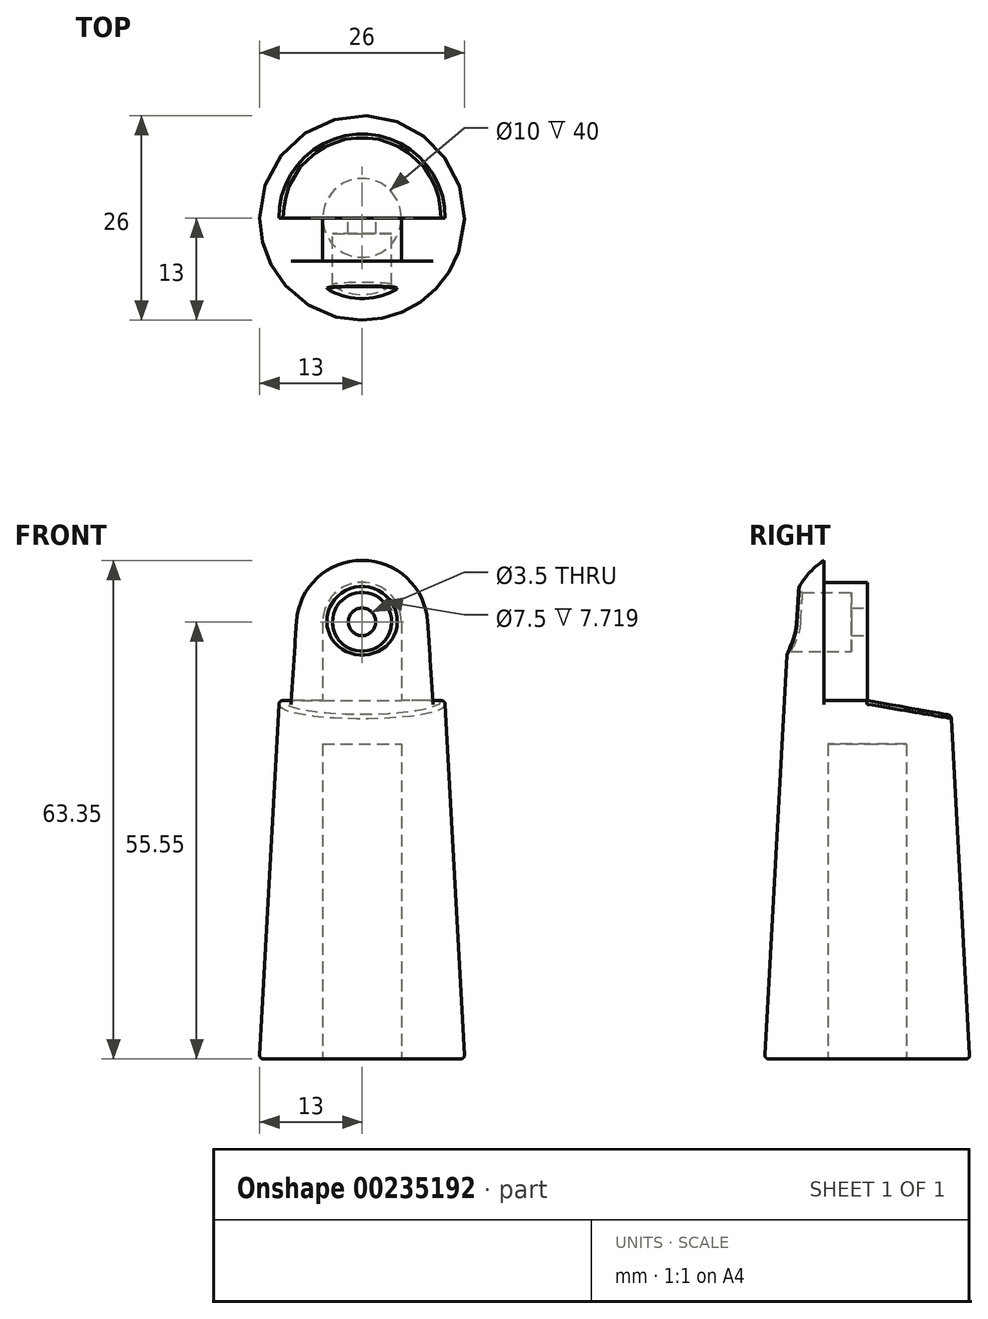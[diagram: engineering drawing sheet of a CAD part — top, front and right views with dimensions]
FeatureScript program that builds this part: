
annotation { "Feature Type Name" : "Feature", "Feature Type Description" : "" }
export const myFeature = defineFeature(function(context is Context, id is Id, definition is map)
    precondition{}
    {
        {
            var Q0;
            Q0=qCreatedBy(makeId("Front.planeOp"),FACE);
            var sketch = newSketch(context, id + "F0", { "sketchPlane" : qUnion([Q0])});
            skArc(sketch, "E0", {"start": v(0, 9.45) * mm, "mid": v(-6.87, 6.71) * mm, "end": v(-9.98, 0) * mm});
            skLineSegment(sketch, "E1", {"start": v(-9.98, 0) * mm, "end": v(-13.03, -55.55) * mm});
            skLineSegment(sketch, "E2", {"start": v(0, 9.45) * mm, "end": v(0, -55.55) * mm});
            skLineSegment(sketch, "E3", {"start": v(-13.03, -55.55) * mm, "end": v(0, -55.55) * mm});
            skSolve(sketch);
        }
        {
            var Q0;
            Q0 = qSketchRegion(id + "F0", true);
            var Q1;
            Q1=sQuery(id+"F0.wireOp",EDGE,"E2");
            revolve(context, id + "F1", {"entities" : qUnion([Q0]), "axis" : qUnion([Q1]), "revolveType" : RevolveType.FULL});
        }
        {
            var Q0;
            Q0=qCreatedBy(makeId("Right.planeOp"),FACE);
            var sketch = newSketch(context, id + "F2", { "sketchPlane" : qUnion([Q0])});
            skLineSegment(sketch, "E4", {"start": v(0, -10) * mm, "end": v(0, 17.7) * mm});
            skLineSegment(sketch, "E5", {"start": v(0, 17.7) * mm, "end": v(18.47, 17.7) * mm});
            skLineSegment(sketch, "E6", {"start": v(18.47, 17.7) * mm, "end": v(18.47, -13.26) * mm});
            skLineSegment(sketch, "E7", {"start": v(18.47, -13.26) * mm, "end": v(0, -10) * mm});
            skSolve(sketch);
        }
        {
            var Q0;
            Q0 = qSketchRegion(id + "F2", true);
            extrude(context, id + "F3", {"entities" : qUnion([Q0]), "operationType" : NewBodyOperationType.REMOVE, "endBound" : BoundingType.THROUGH_ALL, "oppositeDirection" : true, "depth" : 25 * mm, "hasSecondDirection" : true, "secondDirectionBound" : SecondDirectionBoundingType.THROUGH_ALL, "secondDirectionOppositeDirection" : false, "secondDirectionDepth" : 25 * mm});
        }
        {
            var Q0;
            Q0=qCreatedBy(makeId("Front.planeOp"),FACE);
            var sketch = newSketch(context, id + "F4", { "sketchPlane" : qUnion([Q0])});
            skLineSegment(sketch, "E8", {"start": v(0, 5) * mm, "end": v(0, -10) * mm, "construction": true});
            skArc(sketch, "E9", {"start": v(0, 5) * mm, "mid": v(-3.54, 3.54) * mm, "end": v(-5, 0) * mm});
            skLineSegment(sketch, "E10", {"start": v(-5, 0) * mm, "end": v(-5, -10) * mm});
            skLineSegment(sketch, "E11", {"start": v(-5, -10) * mm, "end": v(0, -10) * mm, "construction": true});
            skLineSegment(sketch, "E12.MirrorCS", {"start": v(5, -10) * mm, "end": v(0, -10) * mm, "construction": true});
            skLineSegment(sketch, "E13.MirrorCS", {"start": v(5, 0) * mm, "end": v(5, -10) * mm});
            skArc(sketch, "E14.MirrorCS", {"start": v(0, 5) * mm, "mid": v(3.54, 3.54) * mm, "end": v(5, 0) * mm});
            skLineSegment(sketch, "E15", {"start": v(-5, -10) * mm, "end": v(-22.67, -10) * mm});
            skLineSegment(sketch, "E16", {"start": v(-22.67, -10) * mm, "end": v(-22.67, 27.7) * mm});
            skLineSegment(sketch, "E17", {"start": v(-22.67, 27.7) * mm, "end": v(22.54, 27.7) * mm});
            skLineSegment(sketch, "E18", {"start": v(22.54, 27.7) * mm, "end": v(22.54, -10) * mm});
            skLineSegment(sketch, "E19", {"start": v(22.54, -10) * mm, "end": v(5, -10) * mm});
            skSolve(sketch);
        }
        {
            var Q0;
            Q0 = qSketchRegion(id + "F4", true);
            var Q1;
            Q1 = qConstructionFilter(qBodyType(qCreatedBy(id + "F4" ,EDGE), BodyType.WIRE), ConstructionObject.NO);
            extrude(context, id + "F5", {"entities" : qUnion([Q0]), "operationType" : NewBodyOperationType.REMOVE, "surfaceEntities" : qUnion([Q1]), "depth" : 5.5 * mm});
        }
        {
            var Q0;
            Q0=qCreatedBy(makeId("Front.planeOp"),FACE);
            var sketch = newSketch(context, id + "F6", { "sketchPlane" : qUnion([Q0])});
            skCircle(sketch, "E20", {"center": v(0, 0) * mm, "radius": 1.75 * mm});
            skSolve(sketch);
        }
        {
            var Q0;
            Q0 = qSketchRegion(id + "F6", true);
            extrude(context, id + "F7", {"entities" : qUnion([Q0]), "operationType" : NewBodyOperationType.REMOVE, "endBound" : BoundingType.THROUGH_ALL, "depth" : 25 * mm});
        }
        {
            var Q0;
            Q0=qCreatedBy(makeId("Front.planeOp"),FACE);
            cPlane(context, id + "F8", {"entities" : qUnion([Q0]), "cplaneType" : CPlaneType.OFFSET, "offset" : 2 * mm, "width" : 150 * mm, "height" : 150 * mm});
        }
        {
            var Q0;
            Q0=qCreatedBy(id+"F8.planeOp",FACE);
            var sketch = newSketch(context, id + "F9", { "sketchPlane" : qUnion([Q0])});
            skCircle(sketch, "E21", {"center": v(0, 0) * mm, "radius": 3.75 * mm});
            skSolve(sketch);
        }
        {
            var Q0;
            Q0 = qSketchRegion(id + "F9", true);
            extrude(context, id + "F10", {"entities" : qUnion([Q0]), "operationType" : NewBodyOperationType.REMOVE, "endBound" : BoundingType.THROUGH_ALL, "depth" : 25 * mm});
        }
        {
            var Q0;
            Q0=makeQuery(id+"F5.boolean.opBoolean","INTERSECT",EDGE,{"derivedFrom":[makeQuery(id+"F1.opRevolve","SWEPT_FACE",FACE,{"disambiguationData":[OSD([sQuery(id+"F0.wireOp",EDGE,"E1")])]}),makeQuery(id+"F5.opExtrude","SWEPT_FACE",FACE,{"disambiguationData":[OSD([sQuery(id+"F4.wireOp",EDGE,"E19")])]})]});
            var Q1;
            Q1=makeQuery(id+"F3.boolean.opBoolean","INTERSECT",EDGE,{"derivedFrom":[makeQuery(id+"F1.opRevolve","SWEPT_FACE",FACE,{"disambiguationData":[OSD([sQuery(id+"F0.wireOp",EDGE,"E1")])]}),makeQuery(id+"F3.opExtrude","SWEPT_FACE",FACE,{"disambiguationData":[OSD([sQuery(id+"F2.wireOp",EDGE,"E7")])]})]});
            var Q2;
            Q2=makeQuery(id+"F5.boolean.opBoolean","INTERSECT",EDGE,{"derivedFrom":[makeQuery(id+"F1.opRevolve","SWEPT_FACE",FACE,{"disambiguationData":[OSD([sQuery(id+"F0.wireOp",EDGE,"E1")])]}),makeQuery(id+"F5.opExtrude","SWEPT_FACE",FACE,{"disambiguationData":[OSD([sQuery(id+"F4.wireOp",EDGE,"E15")])]})]});
            var Q3;
            Q3=makeQuery(id+"F5.boolean.opBoolean","INTERSECT",EDGE,{"derivedFrom":[makeQuery(id+"F1.opRevolve","SWEPT_FACE",FACE,{"disambiguationData":[OSD([sQuery(id+"F0.wireOp",EDGE,"E1")])]}),makeQuery(id+"F5.opExtrude","SWEPT_FACE",FACE,{"disambiguationData":[OSD([sQuery(id+"F4.wireOp",EDGE,"E13.MirrorCS")])]})]});
            var Q4;
            Q4=makeQuery(id+"F5.boolean.opBoolean","INTERSECT",EDGE,{"derivedFrom":[makeQuery(id+"F1.opRevolve","SWEPT_FACE",FACE,{"disambiguationData":[OSD([sQuery(id+"F0.wireOp",EDGE,"E0")])]}),makeQuery(id+"F5.opExtrude","SWEPT_FACE",FACE,{"disambiguationData":[OSD([sQuery(id+"F4.wireOp",EDGE,"E9"),sQuery(id+"F4.wireOp",EDGE,"E14.MirrorCS")])]})]});
            var Q5;
            Q5=makeQuery(id+"F5.boolean.opBoolean","INTERSECT",EDGE,{"derivedFrom":[makeQuery(id+"F1.opRevolve","SWEPT_FACE",FACE,{"disambiguationData":[OSD([sQuery(id+"F0.wireOp",EDGE,"E1")])]}),makeQuery(id+"F5.opExtrude","SWEPT_FACE",FACE,{"disambiguationData":[OSD([sQuery(id+"F4.wireOp",EDGE,"E10")])]})]});
            var Q6;
            Q6=makeQuery(id+"F5.boolean.opBoolean","COPY",EDGE,{"derivedFrom":makeQuery(id+"F5.opExtrude","CAP_EDGE",EDGE,{"disambiguationData":[OSD([sQuery(id+"F4.wireOp",EDGE,"E9"),sQuery(id+"F4.wireOp",EDGE,"E14.MirrorCS")])],"isStart":true})});
            var Q7;
            Q7=makeQuery(id+"F5.boolean.opBoolean","COPY",EDGE,{"derivedFrom":makeQuery(id+"F5.opExtrude","CAP_EDGE",EDGE,{"disambiguationData":[OSD([sQuery(id+"F4.wireOp",EDGE,"E13.MirrorCS")])],"isStart":true})});
            var Q8;
            Q8=makeQuery(id+"F5.boolean.opBoolean","COPY",EDGE,{"derivedFrom":makeQuery(id+"F5.opExtrude","CAP_EDGE",EDGE,{"disambiguationData":[OSD([sQuery(id+"F4.wireOp",EDGE,"E10")])],"isStart":true})});
            var Q9;
            Q9=makeQuery(id+"F1.opRevolve","SWEPT_EDGE",EDGE,{"disambiguationData":[OSD([sQuery(id+"F0.wireOp",EDGE,"E1"),sQuery(id+"F0.wireOp",EDGE,"E3")])]});
            var Q10;
            Q10=makeQuery(id+"F10.boolean.opBoolean","INTERSECT",EDGE,{"derivedFrom":[makeQuery(id+"F1.opRevolve","SWEPT_FACE",FACE,{"disambiguationData":[OSD([sQuery(id+"F0.wireOp",EDGE,"E0")])]}),makeQuery(id+"F10.opExtrude","SWEPT_FACE",FACE,{"disambiguationData":[OSD([sQuery(id+"F9.wireOp",EDGE,"E21")])]})]});
            var Q11;
            Q11=makeQuery(id+"F10.boolean.opBoolean","INTERSECT",EDGE,{"derivedFrom":[makeQuery(id+"F1.opRevolve","SWEPT_FACE",FACE,{"disambiguationData":[OSD([sQuery(id+"F0.wireOp",EDGE,"E1")])]}),makeQuery(id+"F10.opExtrude","SWEPT_FACE",FACE,{"disambiguationData":[OSD([sQuery(id+"F9.wireOp",EDGE,"E21")])]})]});
            fillet(context, id + "F11", {"entities" : qUnion([Q0, Q1, Q2, Q3, Q4, Q5, Q6, Q7, Q8, Q9, Q10, Q11]), "radius" : 0.5 * mm, "allowEdgeOverflow" : false});
        }
        {
            var Q0;
            Q0=makeQuery(id+"F1.opRevolve","SWEPT_FACE",FACE,{"disambiguationData":[OSD([sQuery(id+"F0.wireOp",EDGE,"E3")])]});
            var sketch = newSketch(context, id + "F12", { "sketchPlane" : qUnion([Q0])});
            skCircle(sketch, "E22", {"center": v(0, 0) * mm, "radius": 5 * mm});
            skSolve(sketch);
        }
        {
            var Q0;
            Q0 = qSketchRegion(id + "F12", true);
            extrude(context, id + "F13", {"entities" : qUnion([Q0]), "operationType" : NewBodyOperationType.REMOVE, "oppositeDirection" : true, "depth" : 40 * mm});
        }
    });
